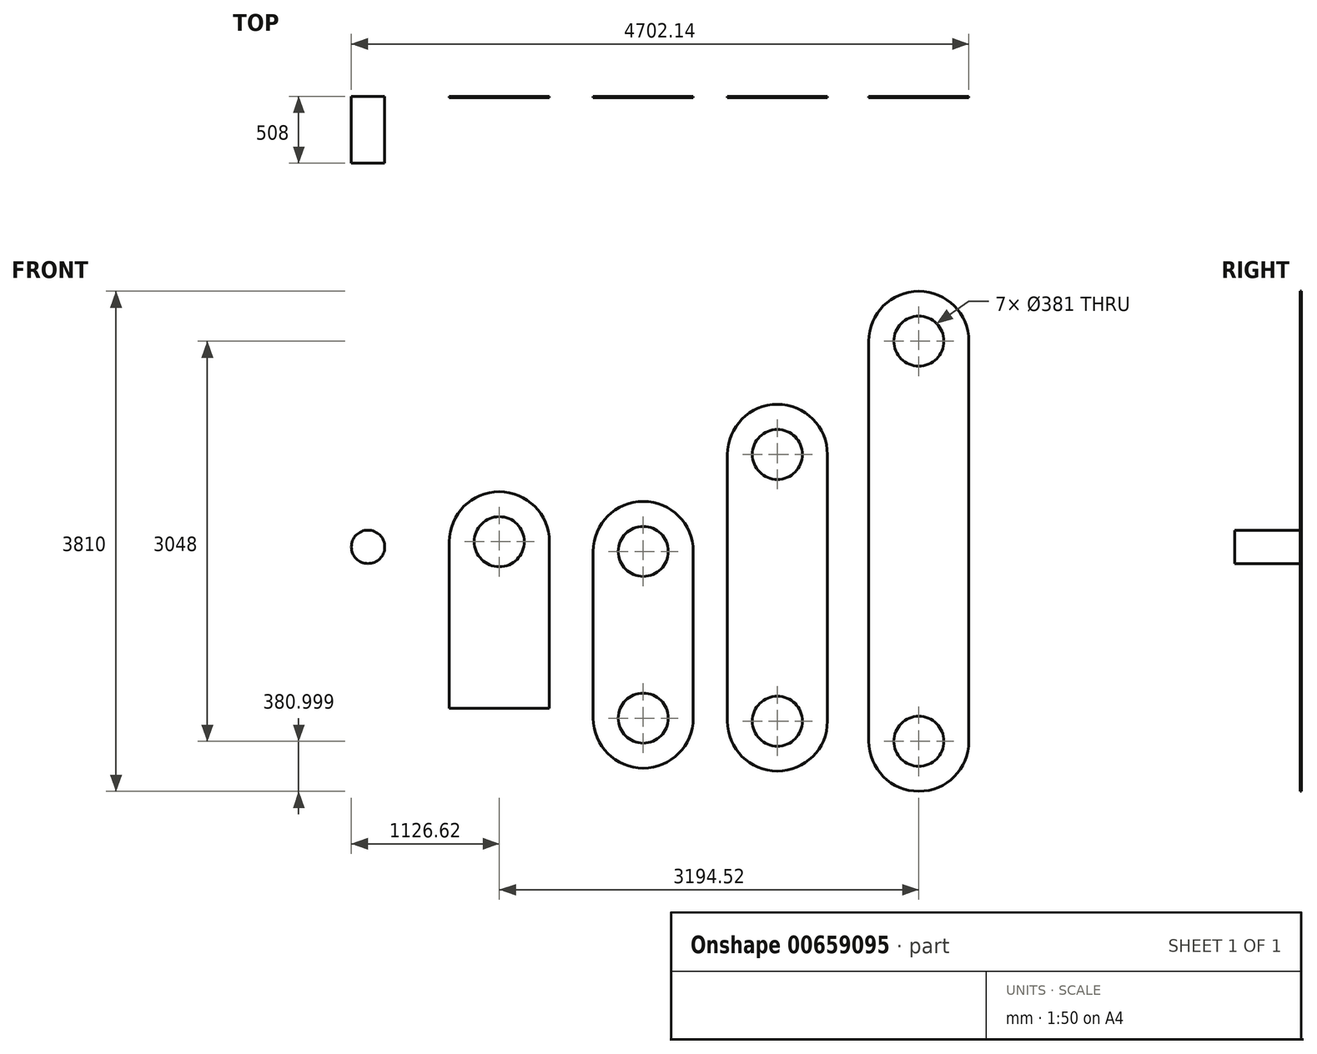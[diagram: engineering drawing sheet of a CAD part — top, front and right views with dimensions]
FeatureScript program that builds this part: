
annotation { "Feature Type Name" : "Feature", "Feature Type Description" : "" }
export const myFeature = defineFeature(function(context is Context, id is Id, definition is map)
    precondition{}
    {
        {
            assignVariable(context, id + "F0", {"name" : "thickness", "anyValue" : 10});
        }
        {
            var Q0;
            Q0=qCreatedBy(makeId("Front.planeOp"),FACE);
            var sketch = newSketch(context, id + "F1", { "sketchPlane" : qUnion([Q0])});
            skCircle(sketch, "E0", {"center": v(-30.98, 39.5) * mm, "radius": 190.5 * mm});
            skArc(sketch, "E1", {"start": v(350.02, 39.5) * mm, "mid": v(-30.98, 420.5) * mm, "end": v(-411.98, 39.5) * mm});
            skLineSegment(sketch, "E2", {"start": v(350.02, 39.5) * mm, "end": v(350.02, -1230.5) * mm});
            skLineSegment(sketch, "E3", {"start": v(350.02, -1230.5) * mm, "end": v(-411.98, -1230.5) * mm});
            skLineSegment(sketch, "E4", {"start": v(-411.98, -1230.5) * mm, "end": v(-411.98, 39.5) * mm});
            skSolve(sketch);
        }
        {
            var Q0;
            Q0=makeQuery(id+"F1.imprint","IMPRINT",FACE,{"disambiguationData":[TD([[makeQuery(id+"F1.imprint","IMPRINT",EDGE,{"derivedFrom":sQuery(id+"F1.wireOp",EDGE,"E0")}),-1.0]])]});
            extrude(context, id + "F2", {"entities" : qUnion([Q0]), "depth" : (getVariable(context, 'thickness')) * mm, "offsetDistance" : 25.4 * mm});
        }
        {
            var Q0;
            Q0=qCreatedBy(makeId("Front.planeOp"),FACE);
            var sketch = newSketch(context, id + "F3", { "sketchPlane" : qUnion([Q0])});
            skCircle(sketch, "E5", {"center": v(1064.85, -34.32) * mm, "radius": 190.5 * mm});
            skArc(sketch, "E6", {"start": v(1445.85, -34.32) * mm, "mid": v(1064.85, 346.68) * mm, "end": v(683.85, -34.32) * mm});
            skLineSegment(sketch, "E7", {"start": v(1445.85, -34.32) * mm, "end": v(1445.85, -1304.32) * mm});
            skLineSegment(sketch, "E8", {"start": v(683.85, -1304.32) * mm, "end": v(683.85, -34.32) * mm});
            skCircle(sketch, "E9", {"center": v(1064.85, -1304.32) * mm, "radius": 190.5 * mm});
            skArc(sketch, "E10", {"start": v(683.85, -1304.32) * mm, "mid": v(1064.85, -1685.32) * mm, "end": v(1445.85, -1304.32) * mm});
            skSolve(sketch);
        }
        {
            var Q0;
            Q0 = qSketchRegion(id + "F3", true);
            extrude(context, id + "F4", {"entities" : qUnion([Q0]), "depth" : (getVariable(context, 'thickness')) * mm, "offsetDistance" : 25.4 * mm});
        }
        {
            var Q0;
            Q0=qCreatedBy(makeId("Front.planeOp"),FACE);
            var sketch = newSketch(context, id + "F5", { "sketchPlane" : qUnion([Q0])});
            skCircle(sketch, "E11", {"center": v(2086.52, 704.38) * mm, "radius": 190.5 * mm});
            skArc(sketch, "E12", {"start": v(2467.52, 704.38) * mm, "mid": v(2086.52, 1085.38) * mm, "end": v(1705.52, 704.38) * mm});
            skLineSegment(sketch, "E13", {"start": v(2467.52, 704.38) * mm, "end": v(2467.52, -1327.62) * mm});
            skLineSegment(sketch, "E14", {"start": v(1705.52, -1327.62) * mm, "end": v(1705.52, 704.38) * mm});
            skArc(sketch, "E15", {"start": v(1705.52, -1327.62) * mm, "mid": v(2086.52, -1708.62) * mm, "end": v(2467.52, -1327.62) * mm});
            skCircle(sketch, "E16", {"center": v(2086.52, -1327.62) * mm, "radius": 190.5 * mm});
            skSolve(sketch);
        }
        {
            var Q0;
            Q0 = qSketchRegion(id + "F5", true);
            extrude(context, id + "F6", {"entities" : qUnion([Q0]), "depth" : (getVariable(context, 'thickness')) * mm, "offsetDistance" : 25.4 * mm});
        }
        {
            var Q0;
            Q0=qCreatedBy(makeId("Front.planeOp"),FACE);
            var sketch = newSketch(context, id + "F7", { "sketchPlane" : qUnion([Q0])});
            skCircle(sketch, "E17", {"center": v(3163.54, 1567.03) * mm, "radius": 190.5 * mm});
            skArc(sketch, "E18", {"start": v(3544.54, 1567.03) * mm, "mid": v(3163.54, 1948.03) * mm, "end": v(2782.54, 1567.03) * mm});
            skLineSegment(sketch, "E19", {"start": v(3544.54, 1567.03) * mm, "end": v(3544.54, -1480.97) * mm});
            skLineSegment(sketch, "E20", {"start": v(2782.54, -1480.97) * mm, "end": v(2782.54, 1567.03) * mm});
            skArc(sketch, "E21", {"start": v(2782.54, -1480.97) * mm, "mid": v(3163.54, -1861.97) * mm, "end": v(3544.54, -1480.97) * mm});
            skCircle(sketch, "E22", {"center": v(3163.54, -1480.97) * mm, "radius": 190.5 * mm});
            skSolve(sketch);
        }
        {
            var Q0;
            Q0 = qSketchRegion(id + "F7", true);
            extrude(context, id + "F8", {"entities" : qUnion([Q0]), "depth" : (getVariable(context, 'thickness')) * mm, "offsetDistance" : 25.4 * mm});
        }
        {
            var Q0;
            Q0=qCreatedBy(makeId("Front.planeOp"),FACE);
            var sketch = newSketch(context, id + "F9", { "sketchPlane" : qUnion([Q0])});
            skCircle(sketch, "E23", {"center": v(-1030.6, 0) * mm, "radius": 127 * mm});
            skSolve(sketch);
        }
        {
            var Q0;
            Q0 = qSketchRegion(id + "F9", true);
            extrude(context, id + "F10", {"entities" : qUnion([Q0]), "depth" : 508 * mm, "offsetDistance" : 25.4 * mm});
        }
    });
